FCSTD DOCUMENT  (FreeCAD 0.18R13588 (Git))
Label: footprint-RF-antenna
License: All rights reserved
LicenseURL: http://en.wikipedia.org/wiki/All_rights_reserved
objects: Sketcher::SketchObject×3, App::Annotation×2, App::DocumentObjectGroup×1
note: 3 computed .brp shape members not serialized (recipe doc carries the construction recipe); baked Part::Feature solids carry a one-line shape summary decoded from their .brp

FEATURE [App::Annotation] Text  label="Ref#_1.0mm"
  LabelText = REF*
  Position = (7,5,0)
FEATURE [App::Annotation] Text001  label="Value#_1.0mm"
  LabelText = dimensions not verified 
  Position = (11,3,0)
FEATURE [Sketcher::SketchObject] Sketch  label="Pads_Poly"
  sketch-geometry (28):
    g0: LineSegment StartX=4.28069 StartY=0.586396 StartZ=0 EndX=4.28069 EndY=2.85575 EndZ=0
    g1: LineSegment StartX=4.28069 StartY=2.85575 StartZ=0 EndX=3.66966 EndY=3.7412 EndZ=0
    g2: LineSegment StartX=3.66966 StartY=3.7412 StartZ=0 EndX=0 EndY=3.7412 EndZ=0
    g3: LineSegment StartX=0 StartY=3.7412 StartZ=0 EndX=0 EndY=5.16028 EndZ=0
    g4: LineSegment StartX=0 StartY=5.16028 StartZ=0 EndX=1.17279 EndY=5.16028 EndZ=0
    g5: LineSegment StartX=1.17279 StartY=5.16028 StartZ=0 EndX=1.17279 EndY=6.09851 EndZ=0
    g6: LineSegment StartX=1.17279 StartY=6.09851 StartZ=0 EndX=-5.6294 EndY=6.09851 EndZ=0
    g7: LineSegment StartX=-5.6294 StartY=6.09851 StartZ=0 EndX=-5.6294 EndY=2.96716 EndZ=0
    g8: LineSegment StartX=-5.6294 StartY=2.96716 StartZ=0 EndX=3.75293 EndY=2.96716 EndZ=0
    g9: LineSegment StartX=3.75293 StartY=2.96716 StartZ=0 EndX=3.75293 EndY=0.586396 EndZ=0
    g10: LineSegment StartX=3.75293 StartY=0.586396 StartZ=0 EndX=2.58014 EndY=0.586396 EndZ=0
    g11: LineSegment StartX=2.58014 StartY=0.586396 StartZ=0 EndX=2.58014 EndY=1.45426 EndZ=0
    g12: LineSegment StartX=2.58014 StartY=1.45426 StartZ=0 EndX=1.17279 EndY=1.45426 EndZ=0
    g13: LineSegment StartX=1.17279 StartY=1.45426 StartZ=0 EndX=1.17279 EndY=0.586396 EndZ=0
    g14: LineSegment StartX=1.17279 StartY=0.586396 StartZ=0 EndX=0 EndY=0.586396 EndZ=0
    g15: LineSegment StartX=0 StartY=0.586396 StartZ=0 EndX=0 EndY=1.45426 EndZ=0
    g16: LineSegment StartX=0 StartY=1.45426 StartZ=0 EndX=-8.18608 EndY=1.45426 EndZ=0
    g17: LineSegment StartX=-8.18608 StartY=1.45426 StartZ=0 EndX=-8.18608 EndY=8.69038 EndZ=0
    g18: LineSegment StartX=-8.18608 StartY=8.69038 StartZ=0 EndX=21.8139 EndY=8.69038 EndZ=0
    g19: LineSegment StartX=21.8139 StartY=8.69038 StartZ=0 EndX=21.8139 EndY=7.27131 EndZ=0
    g20: LineSegment StartX=21.8139 StartY=7.27131 StartZ=0 EndX=2.58014 EndY=7.27131 EndZ=0
    g21: LineSegment StartX=2.58014 StartY=7.27131 StartZ=0 EndX=2.58014 EndY=5.16028 EndZ=0
    g22: LineSegment StartX=2.58014 StartY=5.16028 StartZ=0 EndX=3.75293 EndY=5.16028 EndZ=0
    g23: LineSegment StartX=3.75293 StartY=5.16028 StartZ=0 EndX=3.75293 EndY=4.57154 EndZ=0
    g24: LineSegment StartX=3.75293 StartY=4.57154 StartZ=0 EndX=4.82017 EndY=3.02346 EndZ=0
    g25: LineSegment StartX=4.82017 StartY=3.02346 StartZ=0 EndX=4.82017 EndY=0.586396 EndZ=0
    g26: LineSegment StartX=4.82017 StartY=0.586396 StartZ=0 EndX=4.28069 EndY=0.586396 EndZ=0
    g27: Circle CenterX=0.609678 CenterY=0.998418 CenterZ=0 NormalX=0 NormalY=0 NormalZ=1 AngleXU=0 Radius=0.208388
  constraints (53):
    c: Vertical(g0)
    c: Coincident(g0,g1)
    c: Coincident(g1,g2)
    c: Horizontal(g2)
    c: Coincident(g2,g3)
    c: Vertical(g3)
    c: Coincident(g3,g4)
    c: Horizontal(g4)
    c: Coincident(g4,g5)
    c: Vertical(g5)
    c: Coincident(g5,g6)
    c: Horizontal(g6)
    c: Coincident(g6,g7)
    c: Vertical(g7)
    c: Coincident(g7,g8)
    c: Horizontal(g8)
    c: Coincident(g8,g9)
    c: Vertical(g9)
    c: Coincident(g9,g10)
    c: Horizontal(g10)
    c: Coincident(g10,g11)
    c: Vertical(g11)
    c: Coincident(g11,g12)
    c: Horizontal(g12)
    c: Coincident(g12,g13)
    c: Vertical(g13)
    c: Coincident(g13,g14)
    c: Horizontal(g14)
    c: Coincident(g14,g15)
    c: Vertical(g15)
    c: Coincident(g15,g16)
    c: Horizontal(g16)
    c: Coincident(g16,g17)
    c: Vertical(g17)
    c: Coincident(g17,g18)
    c: Horizontal(g18)
    c: Coincident(g18,g19)
    c: Vertical(g19)
    c: Coincident(g19,g20)
    c: Horizontal(g20)
    c: Coincident(g20,g21)
    c: Vertical(g21)
    c: Coincident(g21,g22)
    c: Horizontal(g22)
    c: Coincident(g22,g23)
    c: Vertical(g23)
    c: Coincident(g23,g24)
    c: Coincident(g24,g25)
    c: Vertical(g25)
    c: Coincident(g25,g26)
    c: Horizontal(g26)
    c: Coincident(g26,g0)
    c: DistanceX(g17,g18) = 30
FEATURE [Sketcher::SketchObject] Sketch001  label="Pads_TH_SMD"
  sketch-geometry (12):
    g0: LineSegment StartX=0 StartY=0.586396 StartZ=0 EndX=1.17279 EndY=0.586396 EndZ=0
    g1: LineSegment StartX=1.17279 StartY=0.586396 StartZ=0 EndX=1.17279 EndY=0 EndZ=0
    g2: LineSegment StartX=1.17279 StartY=0 StartZ=0 EndX=0 EndY=0 EndZ=0
    g3: LineSegment StartX=0 StartY=0 StartZ=0 EndX=0 EndY=0.586396 EndZ=0
    g4: LineSegment StartX=4.28069 StartY=0.586396 StartZ=0 EndX=4.82017 EndY=0.586396 EndZ=0
    g5: LineSegment StartX=4.82017 StartY=0.586396 StartZ=0 EndX=4.82017 EndY=0 EndZ=0
    g6: LineSegment StartX=4.82017 StartY=0 StartZ=0 EndX=4.28069 EndY=0 EndZ=0
    g7: LineSegment StartX=4.28069 StartY=0 StartZ=0 EndX=4.28069 EndY=0.586396 EndZ=0
    g8: LineSegment StartX=2.58014 StartY=0.586396 StartZ=0 EndX=3.75293 EndY=0.586396 EndZ=0
    g9: LineSegment StartX=3.75293 StartY=0.586396 StartZ=0 EndX=3.75293 EndY=0 EndZ=0
    g10: LineSegment StartX=3.75293 StartY=0 StartZ=0 EndX=2.58014 EndY=0 EndZ=0
    g11: LineSegment StartX=2.58014 StartY=0 StartZ=0 EndX=2.58014 EndY=0.586396 EndZ=0
  constraints (24):
    c: Horizontal(g0)
    c: Coincident(g0,g1)
    c: Vertical(g1)
    c: Coincident(g1,g2)
    c: Horizontal(g2)
    c: Coincident(g2,g3)
    c: Vertical(g3)
    c: Coincident(g3,g0)
    c: Horizontal(g4)
    c: Coincident(g4,g5)
    c: Vertical(g5)
    c: Coincident(g5,g6)
    c: Horizontal(g6)
    c: Coincident(g6,g7)
    c: Vertical(g7)
    c: Coincident(g7,g4)
    c: Horizontal(g8)
    c: Coincident(g8,g9)
    c: Vertical(g9)
    c: Coincident(g9,g10)
    c: Horizontal(g10)
    c: Coincident(g10,g11)
    c: Vertical(g11)
    c: Coincident(g11,g8)
FEATURE [Sketcher::SketchObject] Sketch002  label="F_Silks_0.16"
  sketch-geometry (4):
    g0: LineSegment StartX=-9.5 StartY=10 StartZ=0 EndX=23 EndY=10 EndZ=0
    g1: LineSegment StartX=23 StartY=10 StartZ=0 EndX=23 EndY=-1 EndZ=0
    g2: LineSegment StartX=23 StartY=-1 StartZ=0 EndX=-9.5 EndY=-1 EndZ=0
    g3: LineSegment StartX=-9.5 StartY=-1 StartZ=0 EndX=-9.5 EndY=10 EndZ=0
  constraints (8):
    c: Coincident(g0,g1)
    c: Coincident(g1,g2)
    c: Coincident(g2,g3)
    c: Coincident(g3,g0)
    c: Horizontal(g0)
    c: Horizontal(g2)
    c: Vertical(g1)
    c: Vertical(g3)
FEATURE [App::DocumentObjectGroup] Group  label="fp-template-RF-antenna-poly"
  Group = -> [Sketch002,Sketch,Sketch001,Text,Text001]
